# Revit family: Windsor Top Fix
name_source: partatom
category: Generic Models
units: mm (PartAtom-declared; Revit-internal decimal feet)

## family parameters
Always vertical = Yes
Can host rebar = No
Cut with Voids When Loaded = No
Part Type = Normal
Room Calculation Point = No
Round Connector Dimension = Use Diameter
Shared = No
Work Plane-Based = No

## types (5) — shared parameters
Bal Height = 835 mm
HEIGHT = 1100 mm
Manufacturer = UNEX SYSTEMS
Max Post Spacing = 1000 mm  [stored 3.28084 ft]
Post Height = 1076 mm
Top Rail Height = 24 mm  [stored 0.0787402 ft]
URL = WWW.UNEX.CO.NZ
zero-valued in all types: Default Elevation

## per-type parameters (varying)
| type | ART TOP RAIL | Description | Keynote | LENGTH | Model | PPR TOP RAIL | Panel size | Pannel QTY | Post QTY | VRE TOP RAIL | VRR TOP RAIL | VRT TOP RAIL |
| WINDSOR WITH VRE | No | WINDSOR FRAMED BALUSTER WITH VRE TOP RAIL | UNEX SYSTEMS, WINDSOR TOP FIX BALUSTRADE | 5000 mm  [stored 16.4042 ft] | WINDSOR RANGE, TOP FIX (VRE) | No | 693 mm  [stored 2.27362 ft] | 5 | 6 | Yes | No | No |
| WINDSOR WITH PRR | No | WINDSOR FRAMED BALUSTER WITH PRR TOP RAIL | UNEX SYSTEMS, WINDSOR TOP FIX BALUSTRADE | 2500 mm  [stored 8.2021 ft] | WINDSOR RANGE, TOP FIX (PRR) | Yes | 693 mm  [stored 2.27362 ft] | 3 | 4 | No | No | No |
| WINDSOR WITH ART | Yes | WINDSOR FRAMED BALUSTER WITH ART TOP RAIL | UNEX SYSTEMS  WINDSOR TOP FIX BALUSTRADE | 2800 mm  [stored 9.18635 ft] | WINDSOR RANGE, TOP FIX (ART) | No | 693 mm  [stored 2.27362 ft] | 3 | 4 | No | No | No |
| WINDSOR WITH VRT | No | WINDSOR FRAMED BALUSTER WITH VRT TOP RAIL | UNEX SYSTEMS, WINDSOR TOP FIX BALUSTRADE | 1500 mm  [stored 4.92126 ft] | WINDSOR RANGE, TOP FIX (VRT) | No | 843 mm | 2 | 3 | No | No | Yes |
| WINDSOR WITH VRR | No | WINDSOR FRAMED BALUSTER WITH VRR TOP RAIL | UNEX SYSTEMS, WINDSOR TOP FIX BALUSTRADE | 3900 mm  [stored 12.7953 ft] | WINDSOR RANGE, TOP FIX (VRR) | No | 693 mm  [stored 2.27362 ft] | 4 | 5 | No | Yes | No |

note: [stored X ft] marks values corroborated as IEEE doubles in the binary element streams (Revit-internal decimal feet)

## geometry (parser evidence)
native form markers: Sweep x57
no freeform markers — native parametric forms only
